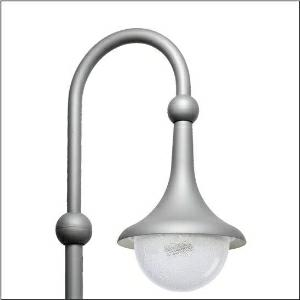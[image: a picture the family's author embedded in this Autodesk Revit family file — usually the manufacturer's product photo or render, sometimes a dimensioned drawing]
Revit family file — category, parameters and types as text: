
# Revit family: grosse_glocke___st1_2a_5xa1563k1b208_bcd9
name_source: partatom
category: Lighting Fixtures
units: mm (PartAtom-declared; Revit-internal decimal feet)

## family parameters
Cut with Voids When Loaded = No
Host = Face
Light Source = No
Part Type = Normal
Room Calculation Point = No
Round Connector Dimension = Use Diameter
Shared = No

## types (1)
- --- (1 x LED, 3380 lm, 23.4 W, 4000K)
    Apparent Load = 23 VA
    CIE Flux Codes = 29 66 94 99 100
    Color Rendering = 70
    Color Temperature = 4000K
    Default Elevation = 1800 mm
    Description = Large Bell, mast luminaire, primary light control with 3 zone facetted reflector, of plastic, silver coated, primary optical cover: enclosure, of PMMA, transparent structured, light distribution: ST1.2a, light emission: direct distribution, primary light characteristic: asymmetric, installation type: suspended mounting, LED High Power LED, rated luminous flux: 3.380 lm, light colour: 740, colour temperature: 4000K, control gear: ECG Plus, control: flexible luminous flux parameterisation, time-dependent luminous flux control, constant luminous flux control, digital communication interface, power reduction, electronic power reduction, mains connection: 220..240V, AC, 50/60Hz, start of lifetime: 23 W, end of lifetime: 24 W, reduction: 12 W, luminaire housing, bell-shaped, of glass-fibre reinforced polyester, coated, Siteco® metallic grey (DB 702S), diameter: 530 mm, height: 695mm, protection rating (complete): IP54, insulation class (complete): insulation class II (safety insulation), certification: CE, ENEC, VDE, impact resistance: IK08, standard-compliant lighting for roads and squares, packaging unit: 1 piece

Light Distribution: ST1.2a
    Height = 695 mm
    Lamp = 1 x LED
    Lamp Light Flux = 3380 lm
    Lamp Power = 23.4 W
    Lamp count = 1
    Length = 530 mm
    Luminous efficacy = 144 lm/W
    Manufacturer = Siteco
    ModVariant = No
    Model = 5XA1563K1B208
    Number of Poles = 1
    OnlyDefault = Yes
    Power Factor = 1
    Product Name = Große Glocke | ST1.2a
    Product group = mast luminaire | pylon annexe
    ProductGroupID = 6200
    Protection Class = Protection class II
    Protection Degree = IP 54
    RLX_Detail_Level = 1
    RlxData = <blob elided: 54641 chars, md5=c26b3495>
    Socket = socket
    Standby Power = 0 W
    System Light Flux = 3380 lm
    System Power = 23 W
    Type Comments = factory setting: luminous flux: 100 % | dim-lin: 254 | 460 mA
    Type Image = l_1005951.jpg
    URL = http://relux.com
    VarID = @adj_130577
    Voltage = 0 V
    Weight = 0.00 kg
    Width = 0 mm  [stored 0 ft]

note: [stored X ft] marks values corroborated as IEEE doubles in the binary element streams (Revit-internal decimal feet)

## geometry (parser evidence)
native form markers: Blend x4, Sweep x11
no freeform markers — native parametric forms only
